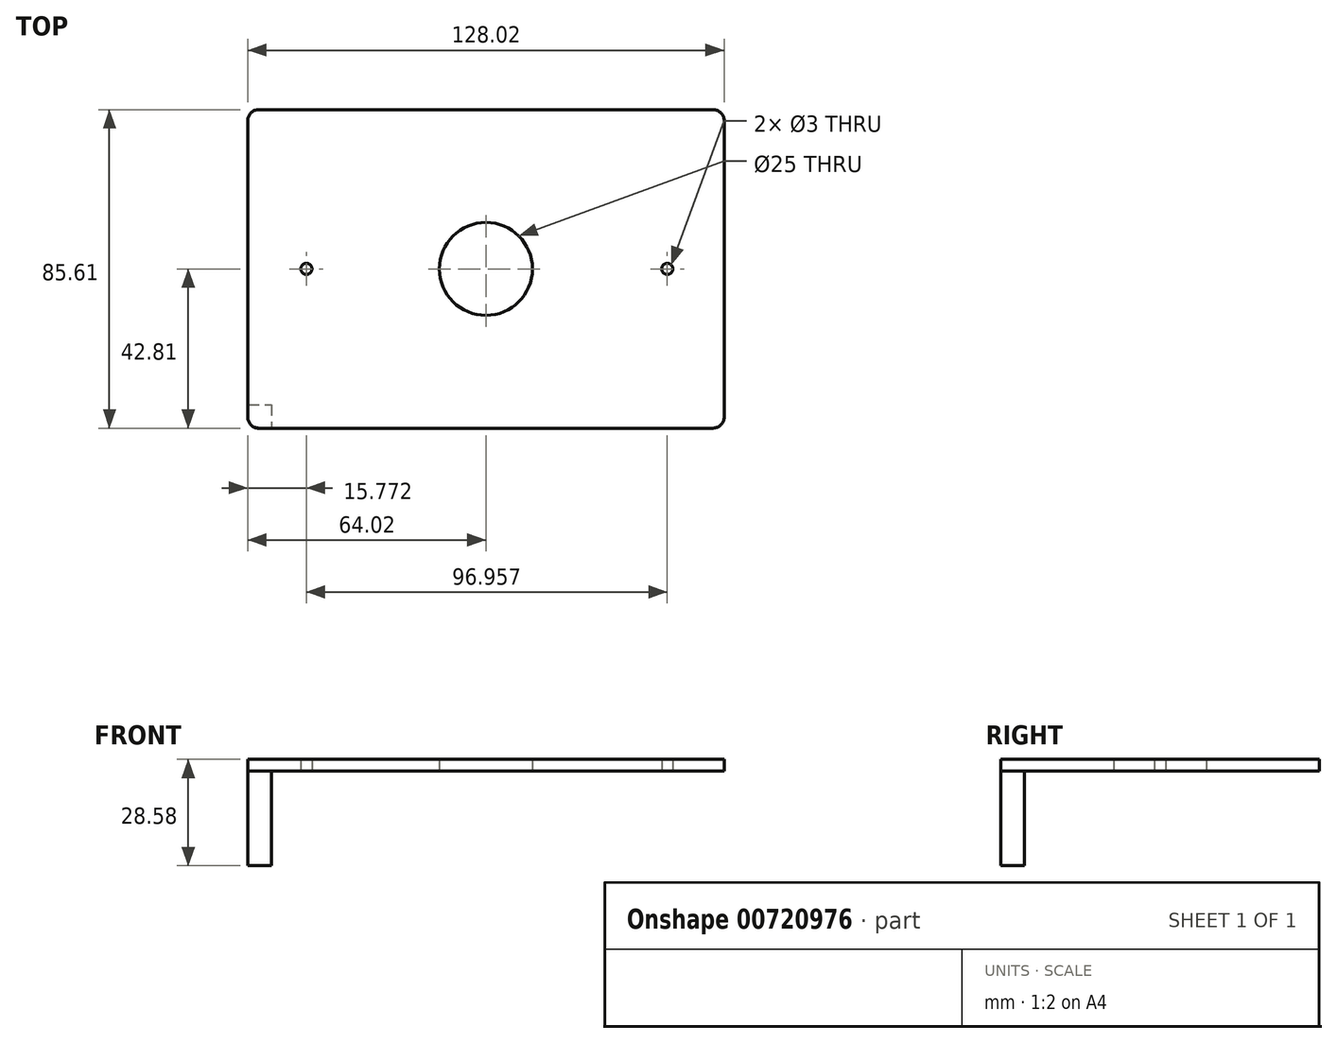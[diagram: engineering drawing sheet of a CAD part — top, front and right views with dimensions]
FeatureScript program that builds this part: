
annotation { "Feature Type Name" : "Feature", "Feature Type Description" : "" }
export const myFeature = defineFeature(function(context is Context, id is Id, definition is map)
    precondition{}
    {
        {
            var Q0;
            Q0=qCreatedBy(makeId("Top.planeOp"),FACE);
            var sketch = newSketch(context, id + "F0", { "sketchPlane" : qUnion([Q0])});
            skLineSegment(sketch, "E0.bottom", {"start": v(-61, 42.8) * mm, "end": v(61, 42.8) * mm});
            skLineSegment(sketch, "E0.top", {"start": v(-61, -42.8) * mm, "end": v(61, -42.8) * mm});
            skLineSegment(sketch, "E0.left", {"start": v(-64, 39.8) * mm, "end": v(-64, -39.8) * mm});
            skLineSegment(sketch, "E0.right", {"start": v(64, 39.8) * mm, "end": v(64, -39.8) * mm});
            skPoint(sketch, "E0.middle", {"position": v(0, 0) * mm});
            skCircle(sketch, "E1", {"center": v(0, 0) * mm, "radius": 12.5 * mm});
            skPoint(sketch, "E2.visualSharp", {"position": v(-64, 42.8) * mm});
            skArc(sketch, "E2.filletArc", {"start": v(-61, 42.8) * mm, "mid": v(-63.12, 41.92) * mm, "end": v(-64, 39.8) * mm});
            skPoint(sketch, "E3.visualSharp", {"position": v(-64, -42.8) * mm});
            skArc(sketch, "E3.filletArc", {"start": v(-64, -39.8) * mm, "mid": v(-63.12, -41.92) * mm, "end": v(-61, -42.8) * mm});
            skPoint(sketch, "E4.visualSharp", {"position": v(64, 42.8) * mm});
            skArc(sketch, "E4.filletArc", {"start": v(64, 39.8) * mm, "mid": v(63.12, 41.92) * mm, "end": v(61, 42.8) * mm});
            skPoint(sketch, "E5.visualSharp", {"position": v(64, -42.8) * mm});
            skArc(sketch, "E5.filletArc", {"start": v(61, -42.8) * mm, "mid": v(63.12, -41.92) * mm, "end": v(64, -39.8) * mm});
            skSolve(sketch);
        }
        {
            var Q0;
            Q0 = qSketchRegion(id + "F0", true);
            extrude(context, id + "F1", {"entities" : qUnion([Q0]), "depth" : 3.17 * mm, "offsetDistance" : 25 * mm});
        }
        {
            var Q0;
            Q0=qCreatedBy(makeId("Top.planeOp"),FACE);
            var sketch = newSketch(context, id + "F2", { "sketchPlane" : qUnion([Q0])});
            skLineSegment(sketch, "E6.bottom", {"start": v(-64.02, -36.46) * mm, "end": v(-57.67, -36.46) * mm});
            skLineSegment(sketch, "E6.top", {"start": v(-61.02, -42.81) * mm, "end": v(-57.67, -42.81) * mm});
            skLineSegment(sketch, "E6.left", {"start": v(-64.02, -36.46) * mm, "end": v(-64.02, -39.81) * mm});
            skLineSegment(sketch, "E6.right", {"start": v(-57.67, -36.46) * mm, "end": v(-57.67, -42.81) * mm});
            skPoint(sketch, "E7.visualSharp", {"position": v(-64.02, -42.81) * mm});
            skArc(sketch, "E7.filletArc", {"start": v(-64.02, -39.81) * mm, "mid": v(-63.15, -41.93) * mm, "end": v(-61.02, -42.81) * mm});
            skSolve(sketch);
        }
        {
            var Q0;
            Q0 = qSketchRegion(id + "F2", true);
            extrude(context, id + "F3", {"entities" : qUnion([Q0]), "operationType" : NewBodyOperationType.ADD, "oppositeDirection" : true, "depth" : 25.4 * mm, "offsetDistance" : 25 * mm});
        }
        {
            var Q0;
            Q0=qCreatedBy(makeId("Top.planeOp"),FACE);
            var sketch = newSketch(context, id + "F4", { "sketchPlane" : qUnion([Q0])});
            skCircle(sketch, "E8", {"center": v(-48.25, 0) * mm, "radius": 1.5 * mm});
            skCircle(sketch, "E9", {"center": v(48.7, 0) * mm, "radius": 1.5 * mm});
            skPoint(sketch, "E9.centerSnap0", {"position": v(48.7, -2) * mm});
            skSolve(sketch);
        }
        {
            var Q0;
            Q0 = qSketchRegion(id + "F4", true);
            extrude(context, id + "F5", {"entities" : qUnion([Q0]), "operationType" : NewBodyOperationType.REMOVE, "depth" : 25 * mm, "offsetDistance" : 25 * mm});
        }
    });
